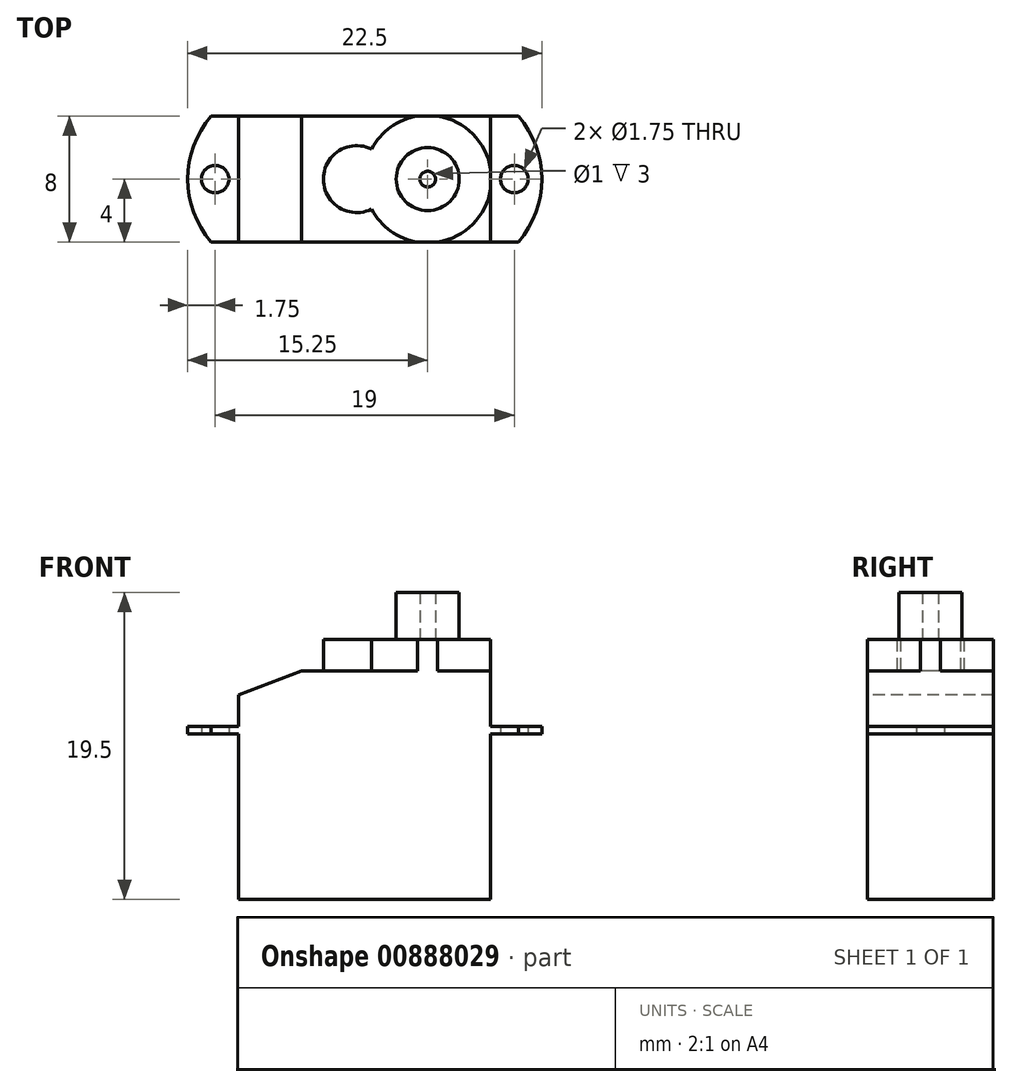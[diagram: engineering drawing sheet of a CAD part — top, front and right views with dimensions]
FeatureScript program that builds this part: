
annotation { "Feature Type Name" : "Feature", "Feature Type Description" : "" }
export const myFeature = defineFeature(function(context is Context, id is Id, definition is map)
    precondition{}
    {
        {
            var Q0;
            Q0=qCreatedBy(makeId("Top.planeOp"),FACE);
            var sketch = newSketch(context, id + "F0", { "sketchPlane" : qUnion([Q0])});
            skLineSegment(sketch, "E0.bottom", {"start": v(8, 4) * mm, "end": v(-8, 4) * mm});
            skLineSegment(sketch, "E0.top", {"start": v(8, -4) * mm, "end": v(-8, -4) * mm});
            skLineSegment(sketch, "E0.left", {"start": v(8, 4) * mm, "end": v(8, -4) * mm});
            skLineSegment(sketch, "E0.right", {"start": v(-8, 4) * mm, "end": v(-8, -4) * mm});
            skPoint(sketch, "E0.middle", {"position": v(0, 0) * mm});
            skSolve(sketch);
        }
        {
            var Q0;
            Q0=qSketchRegion(id+"F0",true);
            extrude(context, id + "F1", {"entities" : qUnion([Q0]), "depth" : 10.5 * mm, "offsetDistance" : 25 * mm});
        }
        {
            var Q0;
            Q0=makeQuery(id+"F1.opExtrude","CAP_FACE",FACE,{"disambiguationData":[OSD([sQuery(id+"F0.wireOp",EDGE,"E0.bottom"),sQuery(id+"F0.wireOp",EDGE,"E0.top"),sQuery(id+"F0.wireOp",EDGE,"E0.left"),sQuery(id+"F0.wireOp",EDGE,"E0.right")])],"isStart":false});
            var sketch = newSketch(context, id + "F2", { "sketchPlane" : qUnion([Q0])});
            skLineSegment(sketch, "E1.bottom", {"start": v(9.75, 4) * mm, "end": v(-9.75, 4) * mm});
            skLineSegment(sketch, "E1.top", {"start": v(9.75, -4) * mm, "end": v(-9.75, -4) * mm});
            skPoint(sketch, "E1.middle", {"position": v(0, 0) * mm});
            skArc(sketch, "E2", {"start": v(-9.75, 4) * mm, "mid": v(-11.25, 0) * mm, "end": v(-9.75, -4) * mm});
            skArc(sketch, "E3", {"start": v(9.75, -4) * mm, "mid": v(11.25, 0) * mm, "end": v(9.75, 4) * mm});
            skCircle(sketch, "E4", {"center": v(-9.5, 0) * mm, "radius": 0.88 * mm});
            skCircle(sketch, "E5", {"center": v(9.5, 0) * mm, "radius": 0.88 * mm});
            skSolve(sketch);
        }
        {
            var Q0;
            Q0=qSketchRegion(id+"F2",true);
            extrude(context, id + "F3", {"entities" : qUnion([Q0]), "operationType" : NewBodyOperationType.ADD, "depth" : 0.5 * mm, "offsetDistance" : 25 * mm});
        }
        {
            var Q0;
            Q0=makeQuery(id+"F3.opExtrude","CAP_FACE",FACE,{"disambiguationData":[OSD([sQuery(id+"F2.wireOp",EDGE,"E1.bottom"),sQuery(id+"F2.wireOp",EDGE,"E1.top"),sQuery(id+"F2.wireOp",EDGE,"E2"),sQuery(id+"F2.wireOp",EDGE,"E3"),sQuery(id+"F2.wireOp",EDGE,"E4"),sQuery(id+"F2.wireOp",EDGE,"E5")])],"isStart":false});
            var sketch = newSketch(context, id + "F4", { "sketchPlane" : qUnion([Q0])});
            skLineSegment(sketch, "E6.bottom", {"start": v(8, 4) * mm, "end": v(-8, 4) * mm});
            skLineSegment(sketch, "E6.top", {"start": v(8, -4) * mm, "end": v(-8, -4) * mm});
            skLineSegment(sketch, "E6.left", {"start": v(8, 4) * mm, "end": v(8, -4) * mm});
            skLineSegment(sketch, "E6.right", {"start": v(-8, 4) * mm, "end": v(-8, -4) * mm});
            skPoint(sketch, "E6.middle", {"position": v(0, 0) * mm});
            skSolve(sketch);
        }
        {
            var Q0;
            Q0=qSketchRegion(id+"F4",true);
            extrude(context, id + "F5", {"entities" : qUnion([Q0]), "operationType" : NewBodyOperationType.ADD, "depth" : 3.5 * mm, "offsetDistance" : 25 * mm});
        }
        {
            var Q0;
            Q0=makeQuery(id+"F5.boolean.opBoolean","MERGE",FACE,{"derivedFrom":[makeQuery(id+"F3.boolean.opBoolean","MERGE",FACE,{"derivedFrom":[makeQuery(id+"F1.opExtrude","SWEPT_FACE",FACE,{"disambiguationData":[OSD([sQuery(id+"F0.wireOp",EDGE,"E0.top")])]}),makeQuery(id+"F3.opExtrude","SWEPT_FACE",FACE,{"disambiguationData":[OSD([sQuery(id+"F2.wireOp",EDGE,"E1.top")])]})]}),makeQuery(id+"F5.opExtrude","SWEPT_FACE",FACE,{"disambiguationData":[OSD([sQuery(id+"F4.wireOp",EDGE,"E6.top")])]})]});
            var sketch = newSketch(context, id + "F6", { "sketchPlane" : qUnion([Q0])});
            skLineSegment(sketch, "E7", {"start": v(-8, 13) * mm, "end": v(-4, 14.5) * mm});
            skLineSegment(sketch, "E8", {"start": v(-4, 14.5) * mm, "end": v(-8, 14.5) * mm});
            skLineSegment(sketch, "E9", {"start": v(-8, 14.5) * mm, "end": v(-8, 13) * mm});
            skSolve(sketch);
        }
        {
            var Q0;
            Q0=qSketchRegion(id+"F6",true);
            extrude(context, id + "F7", {"entities" : qUnion([Q0]), "operationType" : NewBodyOperationType.REMOVE, "oppositeDirection" : true, "depth" : 25 * mm, "offsetDistance" : 25 * mm});
        }
        {
            var Q0;
            Q0=makeQuery(id+"F5.opExtrude","CAP_FACE",FACE,{"disambiguationData":[OSD([sQuery(id+"F4.wireOp",EDGE,"E6.bottom"),sQuery(id+"F4.wireOp",EDGE,"E6.top"),sQuery(id+"F4.wireOp",EDGE,"E6.left"),sQuery(id+"F4.wireOp",EDGE,"E6.right")])],"isStart":false});
            var sketch = newSketch(context, id + "F8", { "sketchPlane" : qUnion([Q0])});
            skCircle(sketch, "E10", {"center": v(4, 0) * mm, "radius": 4.05 * mm});
            skCircle(sketch, "E11", {"center": v(-0.5, 0) * mm, "radius": 2.12 * mm});
            skSolve(sketch);
        }
        {
            var Q0;
            Q0=qSketchRegion(id+"F8",true);
            extrude(context, id + "F9", {"entities" : qUnion([Q0]), "operationType" : NewBodyOperationType.ADD, "depth" : 2 * mm, "offsetDistance" : 25 * mm});
        }
        {
            var Q0;
            {var subQ1=sQuery(id+"F8.wireOp",EDGE,"E10");Q0=makeQuery(id+"F9.boolean.opBoolean","SPLIT",FACE,{"disambiguationData":[TD([makeQuery(id+"F1.opExtrude","SWEPT_FACE",FACE,{"disambiguationData":[OSD([sQuery(id+"F0.wireOp",EDGE,"E0.bottom")])]})])],"derivedFrom":makeQuery(id+"F9.opExtrude","CAP_FACE",FACE,{"disambiguationData":[OSD([subQ1,sQuery(id+"F8.wireOp",EDGE,"E11")])],"isStart":true})});}
            extrude(context, id + "F10", {"entities" : qUnion([Q0]), "operationType" : NewBodyOperationType.REMOVE, "oppositeDirection" : true, "depth" : 25 * mm, "offsetDistance" : 25 * mm});
        }
        {
            var Q0;
            {var subQ1=sQuery(id+"F8.wireOp",EDGE,"E10");Q0=makeQuery(id+"F9.boolean.opBoolean","SPLIT",FACE,{"disambiguationData":[TD([makeQuery(id+"F1.opExtrude","SWEPT_FACE",FACE,{"disambiguationData":[OSD([sQuery(id+"F0.wireOp",EDGE,"E0.top")])]})])],"derivedFrom":makeQuery(id+"F9.opExtrude","CAP_FACE",FACE,{"disambiguationData":[OSD([subQ1,sQuery(id+"F8.wireOp",EDGE,"E11")])],"isStart":true})});}
            extrude(context, id + "F11", {"entities" : qUnion([Q0]), "operationType" : NewBodyOperationType.REMOVE, "oppositeDirection" : true, "depth" : 25 * mm, "offsetDistance" : 25 * mm});
        }
        {
            var Q0;
            {var subQ0=sQuery(id+"F4.wireOp",EDGE,"E6.left");var subQ1=sQuery(id+"F8.wireOp",EDGE,"E10");Q0=makeQuery(id+"F9.boolean.opBoolean","SPLIT",FACE,{"disambiguationData":[TD([makeQuery(id+"F5.opExtrude","SWEPT_FACE",FACE,{"disambiguationData":[OSD([subQ0])]})])],"derivedFrom":makeQuery(id+"F9.opExtrude","CAP_FACE",FACE,{"disambiguationData":[OSD([subQ1,sQuery(id+"F8.wireOp",EDGE,"E11")])],"isStart":true})});}
            extrude(context, id + "F12", {"entities" : qUnion([Q0]), "operationType" : NewBodyOperationType.REMOVE, "oppositeDirection" : true, "depth" : 25 * mm, "offsetDistance" : 25 * mm});
        }
        {
            var Q0;
            Q0=makeQuery(id+"F9.opExtrude","CAP_FACE",FACE,{"disambiguationData":[OSD([sQuery(id+"F8.wireOp",EDGE,"E10"),sQuery(id+"F8.wireOp",EDGE,"E11")])],"isStart":false});
            var sketch = newSketch(context, id + "F13", { "sketchPlane" : qUnion([Q0])});
            skCircle(sketch, "E12", {"center": v(4, 0) * mm, "radius": 2 * mm});
            skCircle(sketch, "E13", {"center": v(4, 0) * mm, "radius": 0.5 * mm});
            skSolve(sketch);
        }
        {
            var Q0;
            Q0=qSketchRegion(id+"F13",true);
            extrude(context, id + "F14", {"entities" : qUnion([Q0]), "operationType" : NewBodyOperationType.ADD, "depth" : 3 * mm, "offsetDistance" : 25 * mm});
        }
    });
